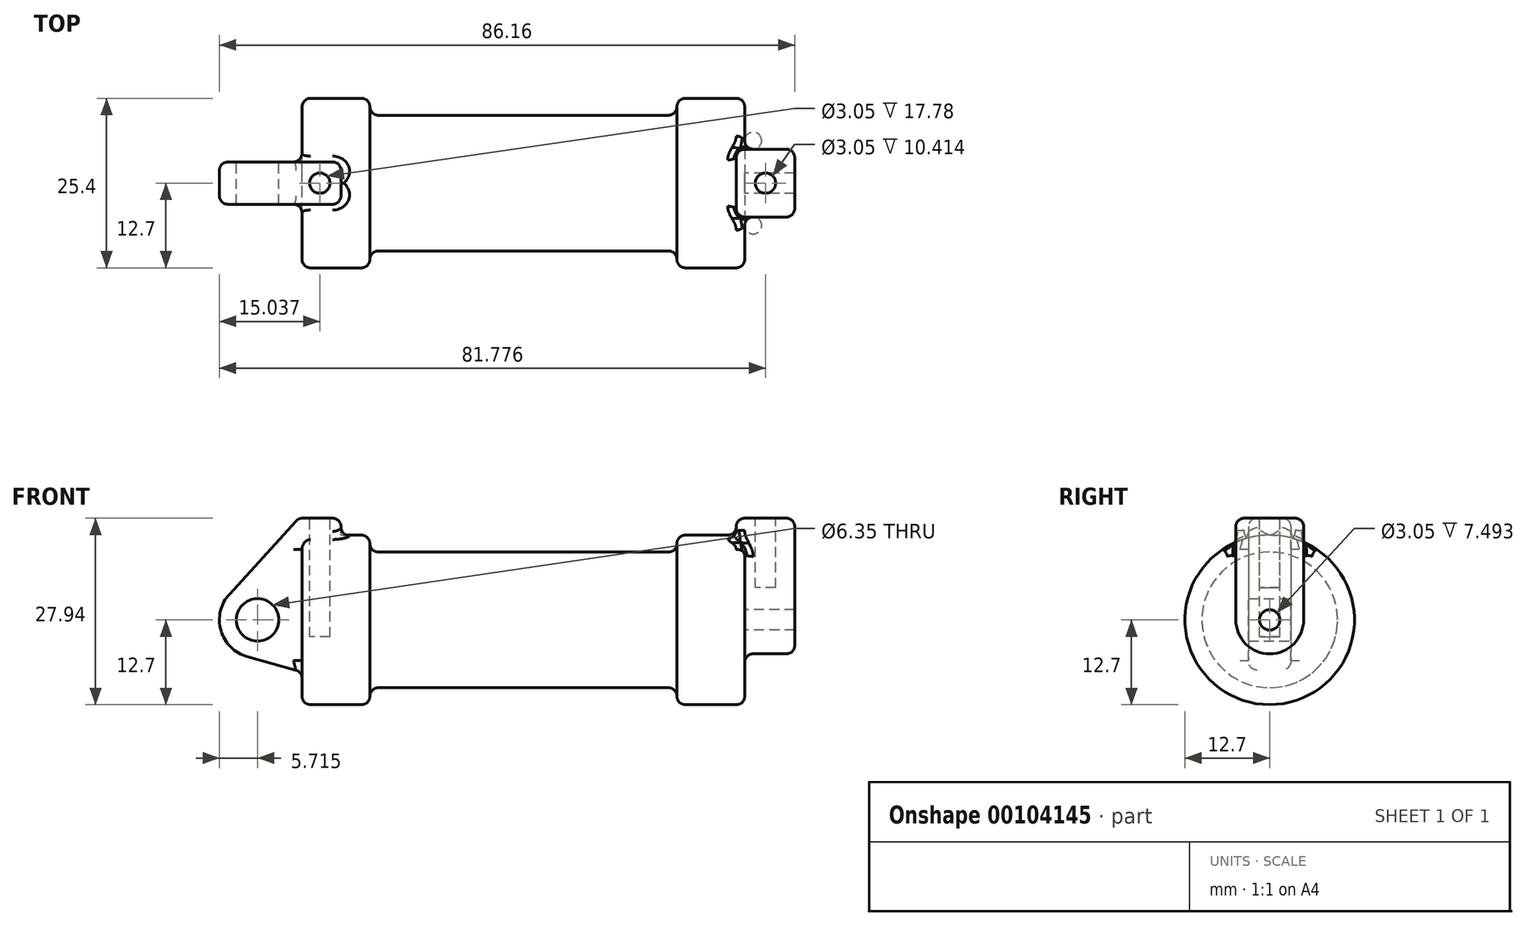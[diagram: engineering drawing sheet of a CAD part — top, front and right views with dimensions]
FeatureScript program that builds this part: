
annotation { "Feature Type Name" : "Feature", "Feature Type Description" : "" }
export const myFeature = defineFeature(function(context is Context, id is Id, definition is map)
    precondition{}
    {
        {
            var Q0;
            Q0=qCreatedBy(makeId("Front.planeOp"),FACE);
            var sketch = newSketch(context, id + "F0", { "sketchPlane" : qUnion([Q0])});
            skLineSegment(sketch, "E0", {"start": v(0, 0) * mm, "end": v(0, 12.7) * mm});
            skLineSegment(sketch, "E1", {"start": v(0, 12.7) * mm, "end": v(10.16, 12.7) * mm});
            skLineSegment(sketch, "E2", {"start": v(10.16, 12.7) * mm, "end": v(10.16, 10.16) * mm});
            skLineSegment(sketch, "E3", {"start": v(10.16, 10.16) * mm, "end": v(56.13, 10.16) * mm});
            skLineSegment(sketch, "E4", {"start": v(56.13, 10.16) * mm, "end": v(56.13, 12.7) * mm});
            skLineSegment(sketch, "E5", {"start": v(56.13, 12.7) * mm, "end": v(66.3, 12.7) * mm});
            skLineSegment(sketch, "E6", {"start": v(66.3, 12.7) * mm, "end": v(66.3, 0) * mm});
            skLineSegment(sketch, "E7", {"start": v(66.3, 0) * mm, "end": v(0, 0) * mm});
            skLineSegment(sketch, "E8", {"start": v(5.84, 15.24) * mm, "end": v(-0.5, 15.24) * mm});
            skLineSegment(sketch, "E9", {"start": v(-0.5, 15.24) * mm, "end": v(-10.88, 3.85) * mm});
            skLineSegment(sketch, "E10", {"start": v(0, 0) * mm, "end": v(-6.65, 0) * mm});
            skCircle(sketch, "E11", {"center": v(-6.65, 0) * mm, "radius": 5.72 * mm});
            skCircle(sketch, "E12", {"center": v(-6.65, 0) * mm, "radius": 3.18 * mm});
            skLineSegment(sketch, "E13", {"start": v(5.84, 15.24) * mm, "end": v(5.84, -9.4) * mm});
            skLineSegment(sketch, "E14", {"start": v(5.84, -9.4) * mm, "end": v(-8.18, -5.5) * mm});
            skSolve(sketch);
        }
        {
            var Q0;
            {var subQ0=sQuery(id+"F0.wireOp",EDGE,"E2");Q0=makeQuery(id+"F0.imprint","IMPRINT",FACE,{"disambiguationData":[TD([[makeQuery(id+"F0.imprint","IMPRINT",EDGE,{"derivedFrom":subQ0}),-1.0]])]});}
            var Q1;
            Q1=sQuery(id+"F0.wireOp",EDGE,"E7");
            revolve(context, id + "F1", {"entities" : qUnion([Q0]), "axis" : qUnion([Q1]), "revolveType" : RevolveType.FULL});
        }
        {
            var Q0;
            {var subQ0=sQuery(id+"F0.wireOp",EDGE,"E0");Q0=makeQuery(id+"F0.imprint","IMPRINT",FACE,{"disambiguationData":[TD([[makeQuery(id+"F0.imprint","IMPRINT",EDGE,{"derivedFrom":subQ0}),-1.0]])]});}
            var Q1;
            Q1=sQuery(id+"F0.wireOp",EDGE,"E7");
            revolve(context, id + "F2", {"operationType" : NewBodyOperationType.ADD, "entities" : qUnion([Q0]), "axis" : qUnion([Q1]), "revolveType" : RevolveType.FULL});
        }
        {
            var Q0;
            {var subQ3=sQuery(id+"F0.wireOp",EDGE,"E0");Q0=makeQuery(id+"F0.imprint","IMPRINT",FACE,{"disambiguationData":[TD([[makeQuery(id+"F0.imprint","IMPRINT",EDGE,{"derivedFrom":subQ3}),1.0]])]});}
            var Q1;
            {var subQ4=sQuery(id+"F0.wireOp",EDGE,"E12");Q1=makeQuery(id+"F0.imprint","IMPRINT",FACE,{"disambiguationData":[TD([[makeQuery(id+"F0.imprint","IMPRINT",EDGE,{"derivedFrom":subQ4}),-1.0]])]});}
            var Q2;
            {var subQ0=sQuery(id+"F0.wireOp",EDGE,"E14");Q2=makeQuery(id+"F0.imprint","IMPRINT",FACE,{"disambiguationData":[TD([[makeQuery(id+"F0.imprint","IMPRINT",EDGE,{"derivedFrom":subQ0}),-1.0]])]});}
            var Q3;
            {var subQ0=sQuery(id+"F0.wireOp",EDGE,"E0");Q3=makeQuery(id+"F0.imprint","IMPRINT",FACE,{"disambiguationData":[TD([[makeQuery(id+"F0.imprint","IMPRINT",EDGE,{"derivedFrom":subQ0}),-1.0]])]});}
            extrude(context, id + "F3", {"entities" : qUnion([Q0, Q1, Q2, Q3]), "operationType" : NewBodyOperationType.ADD, "endBound" : BoundingType.SYMMETRIC, "depth" : 6.35 * mm});
        }
        {
            var Q0;
            Q0=makeQuery(id+"F1.opRevolve","SWEPT_FACE",FACE,{"disambiguationData":[OSD([sQuery(id+"F0.wireOp",EDGE,"E6")])]});
            var sketch = newSketch(context, id + "F4", { "sketchPlane" : qUnion([Q0])});
            skCircle(sketch, "E15", {"center": v(0, 0) * mm, "radius": 1.52 * mm});
            skCircle(sketch, "E16", {"center": v(0, 0) * mm, "radius": 5.08 * mm});
            skLineSegment(sketch, "E17", {"start": v(-5.08, 0) * mm, "end": v(-5.08, 15.24) * mm});
            skLineSegment(sketch, "E18", {"start": v(-5.08, 15.24) * mm, "end": v(5.08, 15.24) * mm});
            skLineSegment(sketch, "E19", {"start": v(5.08, 15.24) * mm, "end": v(5.08, 0) * mm});
            skSolve(sketch);
        }
        {
            var Q0;
            {var subQ0=sQuery(id+"F4.wireOp",EDGE,"E17");var subQ1=sQuery(id+"F4.wireOp",EDGE,"E16");var subQ2=makeQuery(id+"F4.imprint","INTERSECT",VERTEX,{"derivedFrom":[subQ1,subQ0]});Q0=makeQuery(id+"F4.imprint","IMPRINT",FACE,{"disambiguationData":[TD([[makeQuery(id+"F4.imprint","IMPRINT",EDGE,{"disambiguationData":[TD([[subQ2,1.0]])],"derivedFrom":subQ1}),-1.0]])]});}
            var Q1;
            {var subQ0=sQuery(id+"F4.wireOp",EDGE,"E18");Q1=makeQuery(id+"F4.imprint","IMPRINT",FACE,{"disambiguationData":[TD([[makeQuery(id+"F4.imprint","IMPRINT",EDGE,{"derivedFrom":subQ0}),-1.0]])]});}
            var Q2;
            Q2=makeQuery(id+"F4.imprint","IMPRINT",FACE,{"disambiguationData":[TD([[makeQuery(id+"F4.imprint","IMPRINT",EDGE,{"derivedFrom":sQuery(id+"F4.wireOp",EDGE,"E15")}),-1.0]])]});
            extrude(context, id + "F5", {"entities" : qUnion([Q0, Q1, Q2]), "operationType" : NewBodyOperationType.ADD, "depth" : 7.5 * mm, "hasSecondDirection" : true, "secondDirectionOppositeDirection" : true, "secondDirectionDepth" : 1.27 * mm});
        }
        {
            var Q0;
            Q0=makeQuery(id+"F5.opExtrude","SWEPT_FACE",FACE,{"disambiguationData":[OSD([sQuery(id+"F4.wireOp",EDGE,"E18")])]});
            var sketch = newSketch(context, id + "F6", { "sketchPlane" : qUnion([Q0])});
            skPoint(sketch, "E20.centerSnap0", {"position": v(65.02, 0) * mm});
            skCircle(sketch, "E21", {"center": v(69.4, 0) * mm, "radius": 1.52 * mm});
            skPoint(sketch, "E21.centerSnap0", {"position": v(69.4, 5.08) * mm});
            skSolve(sketch);
        }
        {
            var Q0;
            Q0=makeQuery(id+"F3.opExtrude","SWEPT_FACE",FACE,{"disambiguationData":[OSD([sQuery(id+"F0.wireOp",EDGE,"E8")])]});
            var sketch = newSketch(context, id + "F7", { "sketchPlane" : qUnion([Q0])});
            skCircle(sketch, "E22", {"center": v(2.67, 0) * mm, "radius": 1.52 * mm});
            skPoint(sketch, "E22.centerSnap0", {"position": v(2.67, 3.18) * mm});
            skPoint(sketch, "E22.centerSnap1", {"position": v(-0.5, 0) * mm});
            skSolve(sketch);
        }
        {
            var Q0;
            Q0=makeQuery(id+"F7.imprint","IMPRINT",FACE,{"disambiguationData":[TD([[makeQuery(id+"F7.imprint","IMPRINT",EDGE,{"derivedFrom":sQuery(id+"F7.wireOp",EDGE,"E22")}),1.0]])]});
            extrude(context, id + "F8", {"entities" : qUnion([Q0]), "operationType" : NewBodyOperationType.REMOVE, "oppositeDirection" : true, "depth" : 17.78 * mm});
        }
        {
            var Q0;
            Q0=makeQuery(id+"F6.imprint","IMPRINT",FACE,{"disambiguationData":[TD([[makeQuery(id+"F6.imprint","IMPRINT",EDGE,{"derivedFrom":sQuery(id+"F6.wireOp",EDGE,"E21")}),1.0]])]});
            extrude(context, id + "F9", {"entities" : qUnion([Q0]), "operationType" : NewBodyOperationType.REMOVE, "oppositeDirection" : true, "depth" : 10.4 * mm});
        }
        {
            var Q0;
            Q0=makeQuery(id+"F3.opExtrude","CAP_EDGE",EDGE,{"disambiguationData":[OSD([sQuery(id+"F0.wireOp",EDGE,"E8")])],"isStart":false});
            var Q1;
            Q1=makeQuery(id+"F3.opExtrude","SWEPT_EDGE",EDGE,{"disambiguationData":[OSD([sQuery(id+"F0.wireOp",EDGE,"E8"),sQuery(id+"F0.wireOp",EDGE,"E9")])]});
            var Q2;
            Q2=makeQuery(id+"F3.opExtrude","SWEPT_EDGE",EDGE,{"disambiguationData":[OSD([sQuery(id+"F0.wireOp",EDGE,"E8"),sQuery(id+"F0.wireOp",EDGE,"E13")])]});
            var Q3;
            Q3=makeQuery(id+"F3.opExtrude","CAP_EDGE",EDGE,{"disambiguationData":[OSD([sQuery(id+"F0.wireOp",EDGE,"E8")])],"isStart":true});
            var Q4;
            Q4=makeQuery(id+"F3.opExtrude","CAP_EDGE",EDGE,{"disambiguationData":[OSD([sQuery(id+"F0.wireOp",EDGE,"E9")])],"isStart":false});
            var Q5;
            Q5=makeQuery(id+"F3.opExtrude","CAP_EDGE",EDGE,{"disambiguationData":[OSD([sQuery(id+"F0.wireOp",EDGE,"E9")])],"isStart":true});
            var Q6;
            Q6=makeQuery(id+"F3.opExtrude","CAP_EDGE",EDGE,{"disambiguationData":[OSD([sQuery(id+"F0.wireOp",EDGE,"E11")])],"isStart":true});
            var Q7;
            Q7=makeQuery(id+"F3.opExtrude","CAP_EDGE",EDGE,{"disambiguationData":[OSD([sQuery(id+"F0.wireOp",EDGE,"E11")])],"isStart":false});
            var Q8;
            Q8=makeQuery(id+"F3.opExtrude","CAP_EDGE",EDGE,{"disambiguationData":[OSD([sQuery(id+"F0.wireOp",EDGE,"E14")])],"isStart":false});
            var Q9;
            Q9=makeQuery(id+"F3.opExtrude","CAP_EDGE",EDGE,{"disambiguationData":[OSD([sQuery(id+"F0.wireOp",EDGE,"E14")])],"isStart":true});
            var Q10;
            Q10=makeQuery(id+"F2.opRevolve","SWEPT_EDGE",EDGE,{"disambiguationData":[OSD([sQuery(id+"F0.wireOp",EDGE,"E0"),sQuery(id+"F0.wireOp",EDGE,"E1")])]});
            var Q11;
            Q11=makeQuery(id+"F1.opRevolve","SWEPT_EDGE",EDGE,{"disambiguationData":[OSD([sQuery(id+"F0.wireOp",EDGE,"E1"),sQuery(id+"F0.wireOp",EDGE,"E2")])]});
            var Q12;
            Q12=makeQuery(id+"F3.opExtrude","CAP_EDGE",EDGE,{"disambiguationData":[OSD([sQuery(id+"F0.wireOp",EDGE,"E13")])],"isStart":true});
            var Q13;
            {var subQ0=sQuery(id+"F0.wireOp",EDGE,"E1");Q13=makeQuery(id+"F3.boolean.opBoolean","INTERSECT",EDGE,{"derivedFrom":[makeQuery(id+"F2.boolean.opBoolean","MERGE",FACE,{"derivedFrom":[makeQuery(id+"F1.opRevolve","SWEPT_FACE",FACE,{"disambiguationData":[OSD([subQ0])]}),makeQuery(id+"F2.opRevolve","SWEPT_FACE",FACE,{"disambiguationData":[OSD([subQ0])]})]}),makeQuery(id+"F3.opExtrude","CAP_FACE",FACE,{"disambiguationData":[OSD([sQuery(id+"F0.wireOp",EDGE,"E8"),sQuery(id+"F0.wireOp",EDGE,"E9"),sQuery(id+"F0.wireOp",EDGE,"E11"),sQuery(id+"F0.wireOp",EDGE,"E12"),sQuery(id+"F0.wireOp",EDGE,"E13"),sQuery(id+"F0.wireOp",EDGE,"E14")])],"isStart":true})]});}
            var Q14;
            Q14=makeQuery(id+"F3.opExtrude","CAP_EDGE",EDGE,{"disambiguationData":[OSD([sQuery(id+"F0.wireOp",EDGE,"E13")])],"isStart":false});
            var Q15;
            {var subQ0=sQuery(id+"F0.wireOp",EDGE,"E1");Q15=makeQuery(id+"F3.boolean.opBoolean","INTERSECT",EDGE,{"derivedFrom":[makeQuery(id+"F2.boolean.opBoolean","MERGE",FACE,{"derivedFrom":[makeQuery(id+"F1.opRevolve","SWEPT_FACE",FACE,{"disambiguationData":[OSD([subQ0])]}),makeQuery(id+"F2.opRevolve","SWEPT_FACE",FACE,{"disambiguationData":[OSD([subQ0])]})]}),makeQuery(id+"F3.opExtrude","CAP_FACE",FACE,{"disambiguationData":[OSD([sQuery(id+"F0.wireOp",EDGE,"E8"),sQuery(id+"F0.wireOp",EDGE,"E9"),sQuery(id+"F0.wireOp",EDGE,"E11"),sQuery(id+"F0.wireOp",EDGE,"E12"),sQuery(id+"F0.wireOp",EDGE,"E13"),sQuery(id+"F0.wireOp",EDGE,"E14")])],"isStart":false})]});}
            var Q16;
            Q16=makeQuery(id+"F3.boolean.opBoolean","INTERSECT",EDGE,{"derivedFrom":[makeQuery(id+"F2.opRevolve","SWEPT_FACE",FACE,{"disambiguationData":[OSD([sQuery(id+"F0.wireOp",EDGE,"E0")])]}),makeQuery(id+"F3.opExtrude","CAP_FACE",FACE,{"disambiguationData":[OSD([sQuery(id+"F0.wireOp",EDGE,"E8"),sQuery(id+"F0.wireOp",EDGE,"E9"),sQuery(id+"F0.wireOp",EDGE,"E11"),sQuery(id+"F0.wireOp",EDGE,"E12"),sQuery(id+"F0.wireOp",EDGE,"E13"),sQuery(id+"F0.wireOp",EDGE,"E14")])],"isStart":false})]});
            var Q17;
            Q17=makeQuery(id+"F3.boolean.opBoolean","INTERSECT",EDGE,{"derivedFrom":[makeQuery(id+"F2.opRevolve","SWEPT_FACE",FACE,{"disambiguationData":[OSD([sQuery(id+"F0.wireOp",EDGE,"E0")])]}),makeQuery(id+"F3.opExtrude","SWEPT_FACE",FACE,{"disambiguationData":[OSD([sQuery(id+"F0.wireOp",EDGE,"E14")])]})]});
            var Q18;
            Q18=makeQuery(id+"F3.boolean.opBoolean","INTERSECT",EDGE,{"derivedFrom":[makeQuery(id+"F2.opRevolve","SWEPT_FACE",FACE,{"disambiguationData":[OSD([sQuery(id+"F0.wireOp",EDGE,"E0")])]}),makeQuery(id+"F3.opExtrude","CAP_FACE",FACE,{"disambiguationData":[OSD([sQuery(id+"F0.wireOp",EDGE,"E8"),sQuery(id+"F0.wireOp",EDGE,"E9"),sQuery(id+"F0.wireOp",EDGE,"E11"),sQuery(id+"F0.wireOp",EDGE,"E12"),sQuery(id+"F0.wireOp",EDGE,"E13"),sQuery(id+"F0.wireOp",EDGE,"E14")])],"isStart":true})]});
            var Q19;
            Q19=makeQuery(id+"F1.opRevolve","SWEPT_EDGE",EDGE,{"disambiguationData":[OSD([sQuery(id+"F0.wireOp",EDGE,"E2"),sQuery(id+"F0.wireOp",EDGE,"E3")])]});
            var Q20;
            Q20=makeQuery(id+"F5.opExtrude","CAP_EDGE",EDGE,{"disambiguationData":[OSD([sQuery(id+"F4.wireOp",EDGE,"E17")])],"isStart":false});
            var Q21;
            Q21=makeQuery(id+"F5.opExtrude","CAP_EDGE",EDGE,{"disambiguationData":[OSD([sQuery(id+"F4.wireOp",EDGE,"E16")])],"isStart":false});
            var Q22;
            Q22=makeQuery(id+"F5.opExtrude","CAP_EDGE",EDGE,{"disambiguationData":[OSD([sQuery(id+"F4.wireOp",EDGE,"E19")])],"isStart":false});
            var Q23;
            Q23=makeQuery(id+"F5.opExtrude","CAP_EDGE",EDGE,{"disambiguationData":[OSD([sQuery(id+"F4.wireOp",EDGE,"E18")])],"isStart":false});
            var Q24;
            Q24=makeQuery(id+"F5.opExtrude","SWEPT_EDGE",EDGE,{"disambiguationData":[OSD([sQuery(id+"F4.wireOp",EDGE,"E17"),sQuery(id+"F4.wireOp",EDGE,"E18")])]});
            var Q25;
            Q25=makeQuery(id+"F5.opExtrude","CAP_EDGE",EDGE,{"disambiguationData":[OSD([sQuery(id+"F4.wireOp",EDGE,"E17")])],"isStart":true});
            var Q26;
            Q26=makeQuery(id+"F5.boolean.opBoolean","INTERSECT",EDGE,{"derivedFrom":[makeQuery(id+"F1.opRevolve","SWEPT_FACE",FACE,{"disambiguationData":[OSD([sQuery(id+"F0.wireOp",EDGE,"E5")])]}),makeQuery(id+"F5.opExtrude","SWEPT_FACE",FACE,{"disambiguationData":[OSD([sQuery(id+"F4.wireOp",EDGE,"E17")])]})]});
            var Q27;
            Q27=makeQuery(id+"F1.opRevolve","SWEPT_EDGE",EDGE,{"disambiguationData":[OSD([sQuery(id+"F0.wireOp",EDGE,"E5"),sQuery(id+"F0.wireOp",EDGE,"E6")])]});
            var Q28;
            Q28=makeQuery(id+"F5.boolean.opBoolean","INTERSECT",EDGE,{"derivedFrom":[makeQuery(id+"F1.opRevolve","SWEPT_FACE",FACE,{"disambiguationData":[OSD([sQuery(id+"F0.wireOp",EDGE,"E6")])]}),makeQuery(id+"F5.opExtrude","SWEPT_FACE",FACE,{"disambiguationData":[OSD([sQuery(id+"F4.wireOp",EDGE,"E17")])]})]});
            var Q29;
            Q29=makeQuery(id+"F5.boolean.opBoolean","INTERSECT",EDGE,{"derivedFrom":[makeQuery(id+"F1.opRevolve","SWEPT_FACE",FACE,{"disambiguationData":[OSD([sQuery(id+"F0.wireOp",EDGE,"E6")])]}),makeQuery(id+"F5.opExtrude","SWEPT_FACE",FACE,{"disambiguationData":[OSD([sQuery(id+"F4.wireOp",EDGE,"E16")])]})]});
            var Q30;
            Q30=makeQuery(id+"F5.boolean.opBoolean","INTERSECT",EDGE,{"derivedFrom":[makeQuery(id+"F1.opRevolve","SWEPT_FACE",FACE,{"disambiguationData":[OSD([sQuery(id+"F0.wireOp",EDGE,"E6")])]}),makeQuery(id+"F5.opExtrude","SWEPT_FACE",FACE,{"disambiguationData":[OSD([sQuery(id+"F4.wireOp",EDGE,"E19")])]})]});
            var Q31;
            Q31=makeQuery(id+"F5.opExtrude","CAP_EDGE",EDGE,{"disambiguationData":[OSD([sQuery(id+"F4.wireOp",EDGE,"E19")])],"isStart":true});
            var Q32;
            Q32=makeQuery(id+"F5.opExtrude","SWEPT_EDGE",EDGE,{"disambiguationData":[OSD([sQuery(id+"F4.wireOp",EDGE,"E18"),sQuery(id+"F4.wireOp",EDGE,"E19")])]});
            var Q33;
            Q33=makeQuery(id+"F5.boolean.opBoolean","INTERSECT",EDGE,{"derivedFrom":[makeQuery(id+"F1.opRevolve","SWEPT_FACE",FACE,{"disambiguationData":[OSD([sQuery(id+"F0.wireOp",EDGE,"E5")])]}),makeQuery(id+"F5.opExtrude","SWEPT_FACE",FACE,{"disambiguationData":[OSD([sQuery(id+"F4.wireOp",EDGE,"E19")])]})]});
            var Q34;
            Q34=makeQuery(id+"F5.boolean.opBoolean","INTERSECT",EDGE,{"derivedFrom":[makeQuery(id+"F1.opRevolve","SWEPT_FACE",FACE,{"disambiguationData":[OSD([sQuery(id+"F0.wireOp",EDGE,"E5")])]}),makeQuery(id+"F5.opExtrude","CAP_FACE",FACE,{"disambiguationData":[OSD([sQuery(id+"F4.wireOp",EDGE,"E15"),sQuery(id+"F4.wireOp",EDGE,"E16"),sQuery(id+"F4.wireOp",EDGE,"E17"),sQuery(id+"F4.wireOp",EDGE,"E18"),sQuery(id+"F4.wireOp",EDGE,"E19")])],"isStart":true})]});
            var Q35;
            Q35=makeQuery(id+"F5.opExtrude","CAP_EDGE",EDGE,{"disambiguationData":[OSD([sQuery(id+"F4.wireOp",EDGE,"E18")])],"isStart":true});
            var Q36;
            Q36=makeQuery(id+"F1.opRevolve","SWEPT_EDGE",EDGE,{"disambiguationData":[OSD([sQuery(id+"F0.wireOp",EDGE,"E4"),sQuery(id+"F0.wireOp",EDGE,"E5")])]});
            var Q37;
            Q37=makeQuery(id+"F1.opRevolve","SWEPT_EDGE",EDGE,{"disambiguationData":[OSD([sQuery(id+"F0.wireOp",EDGE,"E3"),sQuery(id+"F0.wireOp",EDGE,"E4")])]});
            fillet(context, id + "F10", {"entities" : qUnion([Q0, Q1, Q2, Q3, Q4, Q5, Q6, Q7, Q8, Q9, Q10, Q11, Q12, Q13, Q14, Q15, Q16, Q17, Q18, Q19, Q20, Q21, Q22, Q23, Q24, Q25, Q26, Q27, Q28, Q29, Q30, Q31, Q32, Q33, Q34, Q35, Q36, Q37]), "radius" : 1.27 * mm, "tangentPropagation" : true, "allowEdgeOverflow" : false});
        }
    });
